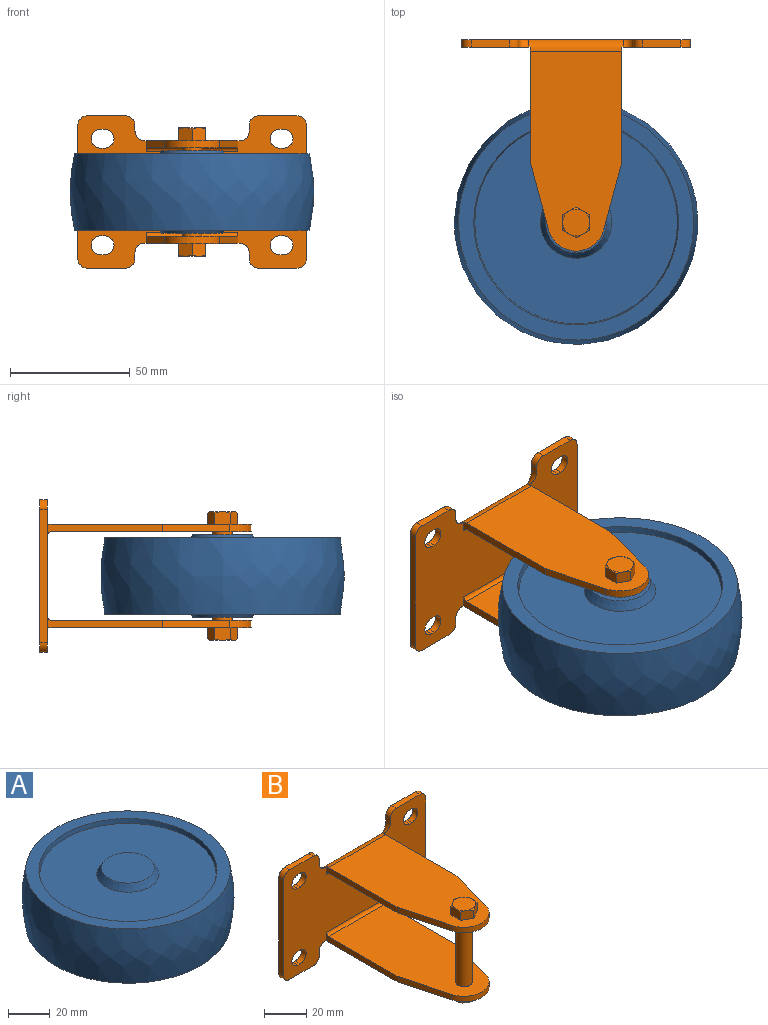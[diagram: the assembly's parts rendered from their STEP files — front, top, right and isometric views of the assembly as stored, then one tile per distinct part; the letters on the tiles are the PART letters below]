
ASSEMBLY  parts=2 mates=1
PART A: 11 faces, bbox 101.6x101.6x34.3 mm
  f0: plane 25.4x25.4mm, normal (0,0,1), area 506.7mm2, adj f1
  f1: cone r=14.9mm half-angle=30deg, axis (0,0,-1), area 381.5mm2, adj f0,f2
  f2: plane 84.45x84.45mm, normal (0,0,1), area 4903.6mm2, adj f1,f3
  f3: cone r=42.67mm half-angle=10deg, axis (0,0,1), area 687.9mm2, adj f2,f4
  f4: plane 98.04x98.04mm, normal (0,0,1), area 1829.2mm2, adj f3,f5
  f5: revolved ~101.6x101.6mm, area 10099.3mm2, adj f4,f6
  f6: plane 98.04x98.04mm, normal (0,0,-1), area 1829.2mm2, adj f5,f7
  f7: cone r=42.22mm half-angle=10deg, axis (0,0,-1), area 687.9mm2, adj f6,f8
  f8: plane 84.45x84.45mm, normal (0,0,-1), area 4903.6mm2, adj f7,f9
  f9: cone r=12.7mm half-angle=30deg, axis (0,0,1), area 381.5mm2, adj f8,f10
  f10: plane 25.4x25.4mm, normal (0,0,-1), area 506.7mm2, adj f9
PART B: 85 faces, bbox 95.8x96.4x64 mm
  f0: plane 47.96x4.76mm, normal (-1,0,0), area 152.7mm2, adj f2,f6,f21,f45,f73,f75
  f1: plane 47.96x4.76mm, normal (1,0,0), area 152.7mm2, adj f2,f6,f25,f45,f73,f75
  f2: plane 83.35x38.1mm, normal (0,0,1), area 2727.7mm2, adj f0,f1,f21,f23,f25,f28,f75
  f3: plane 83.35x38.1mm, normal (0,0,-1), area 2727.7mm2, adj f4,f5,f22,f24,f26,f28,f76
  f4: plane 47.96x4.76mm, normal (-1,0,0), area 152.7mm2, adj f3,f20,f22,f45,f74,f76
  f5: plane 47.96x4.76mm, normal (1,0,0), area 152.7mm2, adj f3,f20,f26,f45,f74,f76
  f6: plane 83.35x38.1mm, normal (0,0,-1), area 2670.2mm2, adj f0,f1,f21,f23,f25,f29,f30,f31
  f7: plane 6.08x5.69mm, normal (-0.5,-0.87,0), area 32mm2, adj f8,f12,f14,f15,f20
  f8: plane 6.08x5.69mm, normal (0.5,-0.87,0), area 32mm2, adj f7,f9,f13,f14,f20
  f9: plane 6.95x5.69mm, normal (1,0,0), area 32mm2, adj f8,f10,f13,f18,f20
  f10: plane 6.08x5.69mm, normal (0.5,0.87,0), area 32mm2, adj f9,f11,f17,f18,f20
  f11: plane 6.08x5.69mm, normal (-0.5,0.87,0), area 32mm2, adj f10,f12,f16,f17,f20
  f12: plane 6.95x5.69mm, normal (-1,0,0), area 32mm2, adj f7,f11,f15,f16,f20
  f13: cone r=5.56mm half-angle=60deg, axis (0,0,-1), area 3mm2, adj f8,f9,f19
  f14: cone r=5.56mm half-angle=60deg, axis (0,0,-1), area 3mm2, adj f7,f8,f19
  f15: cone r=5.56mm half-angle=60deg, axis (0,0,-1), area 3mm2, adj f7,f12,f19
  f16: cone r=5.56mm half-angle=60deg, axis (0,0,-1), area 3mm2, adj f11,f12,f19
  f17: cone r=5.56mm half-angle=60deg, axis (0,0,-1), area 3mm2, adj f10,f11,f19
  f18: cone r=5.56mm half-angle=60deg, axis (0,0,-1), area 3mm2, adj f9,f10,f19
  f19: plane 11.11x11.11mm, normal (0,0,1), area 97mm2, adj f13,f14,f15,f16,f17,f18
  f20: plane 83.35x38.1mm, normal (0,0,1), area 2670.2mm2, adj f4,f5,f7,f8,f9,f10,f11,f12
  f21: plane 28.15x7.54mm, normal (-0.97,-0.26,0), area 92.5mm2, adj f0,f2,f6,f23
  f22: plane 28.15x7.54mm, normal (-0.97,-0.26,0), area 92.5mm2, adj f3,f4,f20,f24
  f23: cylinder r=11.91mm len=23.01mm, axis (0,0,-1), area 99mm2, adj f2,f6,f21,f25
  f24: cylinder r=11.91mm len=23.01mm, axis (0,0,-1), area 99mm2, adj f3,f20,f22,f26
  f25: plane 28.15x7.54mm, normal (0.97,-0.26,0), area 92.5mm2, adj f1,f2,f6,f23
  f26: plane 28.15x7.54mm, normal (0.97,-0.26,0), area 92.5mm2, adj f3,f5,f20,f24
  f27: plane 95.25x63.5mm, normal (0,1,0), area 4392.4mm2, adj f42,f43,f44,f46,f47,f48,f49,f50
  f28: cylinder r=3.97mm len=36.83mm, axis (0,0,-1), area 918.4mm2, adj f2,f3
  f29: plane 6.08x5.69mm, normal (-0.5,-0.87,0), area 32mm2, adj f6,f30,f34,f36,f37
  f30: plane 6.08x5.69mm, normal (0.5,-0.87,0), area 32mm2, adj f6,f29,f31,f35,f36
  f31: plane 6.95x5.69mm, normal (1,0,0), area 32mm2, adj f6,f30,f32,f35,f40
  f32: plane 6.08x5.69mm, normal (0.5,0.87,0), area 32mm2, adj f6,f31,f33,f39,f40
  f33: plane 6.08x5.69mm, normal (-0.5,0.87,0), area 32mm2, adj f6,f32,f34,f38,f39
  f34: plane 6.95x5.69mm, normal (-1,0,0), area 32mm2, adj f6,f29,f33,f37,f38
  f35: cone r=5.56mm half-angle=60deg, axis (0,0,1), area 3mm2, adj f30,f31,f41
  f36: cone r=5.56mm half-angle=60deg, axis (0,0,1), area 3mm2, adj f29,f30,f41
  f37: cone r=5.56mm half-angle=60deg, axis (0,0,1), area 3mm2, adj f29,f34,f41
  f38: cone r=5.56mm half-angle=60deg, axis (0,0,1), area 3mm2, adj f33,f34,f41
  f39: cone r=5.56mm half-angle=60deg, axis (0,0,1), area 3mm2, adj f32,f33,f41
  f40: cone r=5.56mm half-angle=60deg, axis (0,0,1), area 3mm2, adj f31,f32,f41
  f41: plane 11.11x11.11mm, normal (0,0,-1), area 97mm2, adj f35,f36,f37,f38,f39,f40
  f42: plane 15.89x3.18mm, normal (0,0,-1), area 50.4mm2, adj f27,f45,f48,f83
  f43: plane 15.89x3.18mm, normal (0,0,1), area 50.4mm2, adj f27,f45,f46,f84
  f44: plane 15.89x3.18mm, normal (0,0,1), area 50.4mm2, adj f27,f45,f52,f82
  f45: plane 95.44x63.69mm, normal (0,-1,0), area 4451.3mm2, adj f0,f1,f4,f5,f42,f43,f44,f46
  f46: cylinder r=3.96mm len=3.96mm, axis (0,1,0), area 19.8mm2, adj f27,f43,f45,f47
  f47: plane 55.58x3.18mm, normal (-1,0,0), area 176.5mm2, adj f27,f45,f46,f48
  f48: cylinder r=3.96mm len=3.96mm, axis (0,1,0), area 19.8mm2, adj f27,f42,f45,f47
  f49: plane 15.89x3.18mm, normal (0,0,-1), area 50.4mm2, adj f27,f45,f50,f81
  f50: cylinder r=3.96mm len=3.96mm, axis (0,1,0), area 19.8mm2, adj f27,f45,f49,f51
  f51: plane 55.58x3.18mm, normal (1,0,0), area 176.5mm2, adj f27,f45,f50,f52
  f52: cylinder r=3.96mm len=3.96mm, axis (0,1,0), area 19.8mm2, adj f27,f44,f45,f51
  f53: cylinder r=3.97mm len=7.94mm, axis (0,1,0), area 39.6mm2, adj f27,f45,f54,f56
  f54: plane 3.18x1.59mm, normal (0,0,1), area 5mm2, adj f27,f45,f53,f55
  f55: cylinder r=3.97mm len=7.94mm, axis (0,1,0), area 39.6mm2, adj f27,f45,f54,f56
  f56: plane 3.18x1.59mm, normal (0,0,-1), area 5mm2, adj f27,f45,f53,f55
  f57: cylinder r=3.97mm len=7.94mm, axis (0,1,0), area 39.6mm2, adj f27,f45,f58,f60
  f58: plane 3.18x1.59mm, normal (0,0,1), area 5mm2, adj f27,f45,f57,f59
  f59: cylinder r=3.97mm len=7.94mm, axis (0,1,0), area 39.6mm2, adj f27,f45,f58,f60
  f60: plane 3.18x1.59mm, normal (0,0,-1), area 5mm2, adj f27,f45,f57,f59
  f61: cylinder r=3.97mm len=7.94mm, axis (0,1,0), area 39.6mm2, adj f27,f45,f62,f64
  f62: plane 3.18x1.59mm, normal (0,0,1), area 5mm2, adj f27,f45,f61,f63
  f63: cylinder r=3.97mm len=7.94mm, axis (0,1,0), area 39.6mm2, adj f27,f45,f62,f64
  f64: plane 3.18x1.59mm, normal (0,0,-1), area 5mm2, adj f27,f45,f61,f63
  f65: cylinder r=3.97mm len=7.94mm, axis (0,1,0), area 39.6mm2, adj f27,f45,f66,f68
  f66: plane 3.18x1.59mm, normal (0,0,-1), area 5mm2, adj f27,f45,f65,f67
  f67: cylinder r=3.97mm len=7.94mm, axis (0,1,0), area 39.6mm2, adj f27,f45,f66,f68
  f68: plane 3.18x1.59mm, normal (0,0,1), area 5mm2, adj f27,f45,f65,f67
  f69: plane 3.65x3.18mm, normal (1,0,0), area 9.2mm2, adj f27,f45,f80,f84
  f70: plane 3.65x3.18mm, normal (-1,0,0), area 9.2mm2, adj f27,f45,f79,f82
  f71: plane 3.65x3.18mm, normal (1,0,0), area 9.2mm2, adj f27,f45,f77,f83
  f72: plane 3.65x3.18mm, normal (-1,0,0), area 9.2mm2, adj f27,f45,f78,f81
  f73: cylinder r=4.76mm len=39.7mm, axis (-1,0,0), area 294.4mm2, adj f0,f1,f6,f27,f45,f77,f78
  f74: cylinder r=4.76mm len=39.7mm, axis (1,0,0), area 294.4mm2, adj f4,f5,f20,f27,f45,f79,f80
  f75: cylinder r=1.59mm len=38.1mm, axis (-1,0,0), area 95mm2, adj f0,f1,f2,f45
  f76: cylinder r=1.59mm len=38.1mm, axis (1,0,0), area 95mm2, adj f3,f4,f5,f45
  f77: torus R=8.72mm, axis (-1,0,0), area 26.1mm2, adj f27,f45,f71,f73
  f78: torus R=8.72mm, axis (1,0,0), area 26.1mm2, adj f27,f45,f72,f73
  f79: torus R=8.72mm, axis (-1,0,0), area 26.1mm2, adj f27,f45,f70,f74
  f80: torus R=8.72mm, axis (1,0,0), area 26.1mm2, adj f27,f45,f69,f74
  f81: cylinder r=3.96mm len=3.96mm, axis (0,-1,0), area 19.8mm2, adj f27,f45,f49,f72
  f82: cylinder r=3.96mm len=3.96mm, axis (0,1,0), area 19.8mm2, adj f27,f44,f45,f70
  f83: cylinder r=3.96mm len=3.96mm, axis (0,1,0), area 19.8mm2, adj f27,f42,f45,f71
  f84: cylinder r=3.96mm len=3.96mm, axis (0,-1,0), area 19.8mm2, adj f27,f43,f45,f69
PLACE A at identity
PLACE B at identity
MATE fastened A.f1 <-> B.f13  axis (0,0,-1) through (0,-76.2,0)mm
